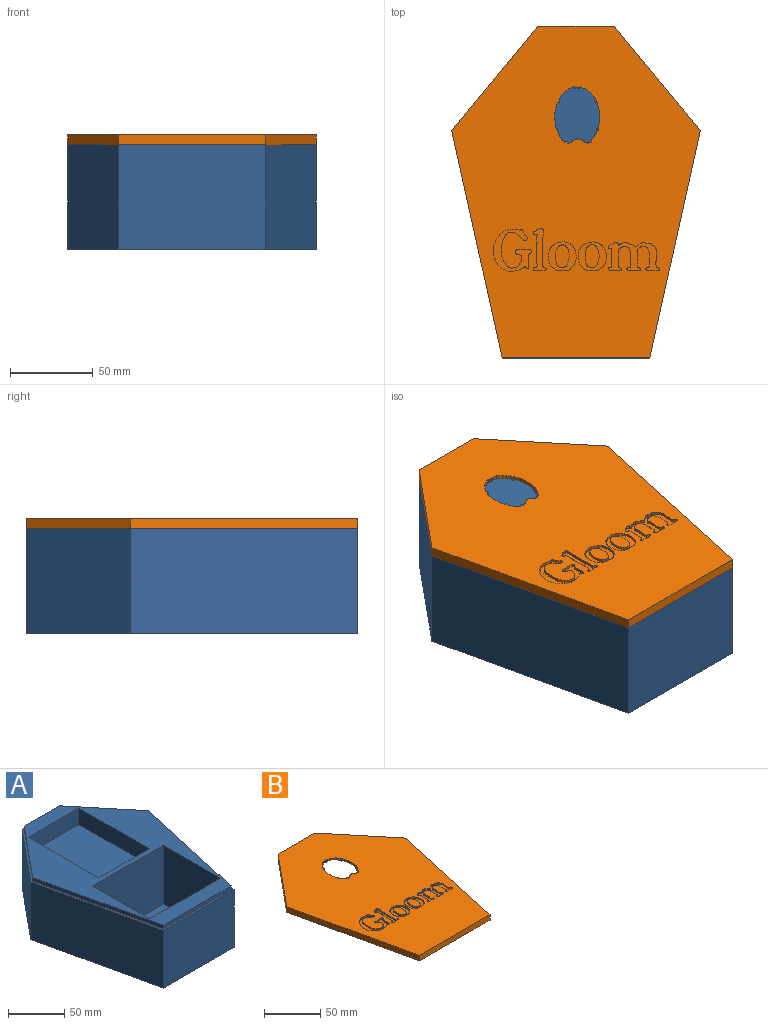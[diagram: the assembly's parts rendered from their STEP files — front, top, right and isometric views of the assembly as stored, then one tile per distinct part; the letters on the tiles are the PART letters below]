
ASSEMBLY  parts=2 mates=1
PART A: 25 faces, bbox 150x200x67 mm
  f0: plane 196x145.67mm, normal (0,0,1), area 9301.1mm2, adj f1,f2,f3,f4,f6,f7,f8,f9
  f1: plane 89x18mm, normal (1,0,0), area 1602mm2, adj f0,f2,f4,f5
  f2: plane 64x18mm, normal (0,1,0), area 1152mm2, adj f0,f1,f3,f5
  f3: plane 89x18mm, normal (-1,0,0), area 1602mm2, adj f0,f2,f4,f5
  f4: plane 64x18mm, normal (0,-1,0), area 1152mm2, adj f0,f1,f3,f5
  f5: plane 89x64mm, normal (0,0,1), area 5696mm2, adj f1,f2,f3,f4
  f6: plane 72x64mm, normal (1,0,0), area 4608mm2, adj f0,f7,f9,f10
  f7: plane 89x64mm, normal (0,1,0), area 5696mm2, adj f0,f6,f8,f10
  f8: plane 72x64mm, normal (-1,0,0), area 4608mm2, adj f0,f7,f9,f10
  f9: plane 89x64mm, normal (0,-1,0), area 5696mm2, adj f0,f6,f8,f10
  f10: plane 89x72mm, normal (0,0,1), area 6408mm2, adj f6,f7,f8,f9
  f11: plane 134.56x29.94mm, normal (0.98,-0.22,0), area 551.4mm2, adj f0,f12,f16,f17
  f12: plane 85.79x4mm, normal (0,-1,0), area 343.2mm2, adj f0,f11,f13,f17
  f13: plane 134.56x29.94mm, normal (-0.98,-0.22,0), area 551.4mm2, adj f0,f12,f14,f17
  f14: plane 61.44x50.74mm, normal (-0.77,0.64,0), area 318.7mm2, adj f0,f13,f15,f17
  f15: plane 44.18x4mm, normal (0,1,0), area 176.7mm2, adj f0,f14,f16,f17
  f16: plane 61.44x50.74mm, normal (0.77,0.64,0), area 318.7mm2, adj f0,f11,f15,f17
  f17: plane 200x150mm, normal (0,0,1), area 1144.2mm2, adj f11,f12,f13,f14,f15,f16,f19,f20
  f18: plane 200x150mm, normal (0,0,-1), area 22549.3mm2, adj f19,f20,f21,f22,f23,f24
  f19: plane 63x46.07mm, normal (0,1,0), area 2902.2mm2, adj f17,f18,f20,f24
  f20: plane 63x62.92mm, normal (0.77,0.64,0), area 5141.2mm2, adj f17,f18,f19,f21
  f21: plane 137.08x63mm, normal (0.98,-0.22,0), area 8847.1mm2, adj f17,f18,f20,f22
  f22: plane 89x63mm, normal (0,-1,0), area 5607mm2, adj f17,f18,f21,f23
  f23: plane 137.08x63mm, normal (-0.98,-0.22,0), area 8847.1mm2, adj f17,f18,f22,f24
  f24: plane 63x62.92mm, normal (-0.77,0.64,0), area 5141.2mm2, adj f17,f18,f19,f23
PART B: 30 faces, bbox 150x200x6 mm
  f0: plane 200x150mm, normal (0,0,1), area 21755.4mm2, adj f1,f2,f3,f4,f5,f6,f15,f17
  f1: plane 137.08x30.5mm, normal (0.98,-0.22,0), area 842.6mm2, adj f0,f2,f6,f7
  f2: plane 62.92x51.97mm, normal (0.77,0.64,0), area 489.6mm2, adj f0,f1,f3,f7
  f3: plane 46.07x6mm, normal (0,1,0), area 276.4mm2, adj f0,f2,f4,f7
  f4: plane 62.92x51.97mm, normal (-0.77,0.64,0), area 489.6mm2, adj f0,f3,f5,f7
  f5: plane 137.08x30.5mm, normal (-0.98,-0.22,0), area 842.6mm2, adj f0,f4,f6,f7
  f6: plane 89x6mm, normal (0,-1,0), area 534mm2, adj f0,f1,f5,f7
  f7: plane 200x150mm, normal (0,0,-1), area 1144.2mm2, adj f1,f2,f3,f4,f5,f6,f8,f9
  f8: plane 134.56x29.94mm, normal (0.98,0.22,0), area 551.4mm2, adj f7,f9,f13,f14
  f9: plane 61.44x50.74mm, normal (0.77,-0.64,0), area 318.7mm2, adj f7,f8,f10,f14
  f10: plane 44.18x4mm, normal (0,-1,0), area 176.7mm2, adj f7,f9,f11,f14
  f11: plane 61.44x50.74mm, normal (-0.77,-0.64,0), area 318.7mm2, adj f7,f10,f12,f14
  f12: plane 134.56x29.94mm, normal (-0.98,0.22,0), area 551.4mm2, adj f7,f11,f13,f14
  f13: plane 85.79x4mm, normal (0,1,0), area 343.2mm2, adj f7,f8,f12,f14
  f14: plane 196x145.67mm, normal (0,0,-1), area 20810.6mm2, adj f8,f9,f10,f11,f12,f13,f29
  f15: extruded ~25.3x7.49mm, area 93.5mm2, adj f0,f16
  f16: plane 25.47x7.78mm, normal (0,0,1), area 103.3mm2, adj f15
  f17: extruded ~30.46x16.9mm, area 228.7mm2, adj f0,f18
  f18: plane 31.26x17.65mm, normal (0,0,1), area 98.7mm2, adj f17
  f19: extruded ~17.5x16.72mm, area 82.5mm2, adj f0,f21
  f20: extruded ~13.84x8.29mm, area 53.7mm2, adj f21,f28
  f21: plane 17.73x17.04mm, normal (0,0,1), area 147mm2, adj f19,f20
  f22: extruded ~14.08x8.39mm, area 54.3mm2, adj f24,f25
  f23: extruded ~17.45x16.86mm, area 82.6mm2, adj f0,f24
  f24: plane 17.57x17.06mm, normal (0,0,1), area 145.7mm2, adj f22,f23
  f25: plane 14.25x8.56mm, normal (0,0,1), area 95mm2, adj f22
  f26: extruded ~25.27x23.06mm, area 202.7mm2, adj f0,f27
  f27: plane 26.05x23.65mm, normal (0,0,1), area 241.2mm2, adj f26
  f28: plane 14.06x8.51mm, normal (0,0,1), area 92.6mm2, adj f20
  f29: extruded ~33.59x27.13mm, area 248.2mm2, adj f0,f14
PLACE A t=(-17.01,33.8,-23.69)mm fixed
PLACE B t=(-17.01,33.8,-27.69)mm
MATE slider B.f14 <-> A.f0  axis (0,0,-1) through (5.09,94.72,43.31)mm
